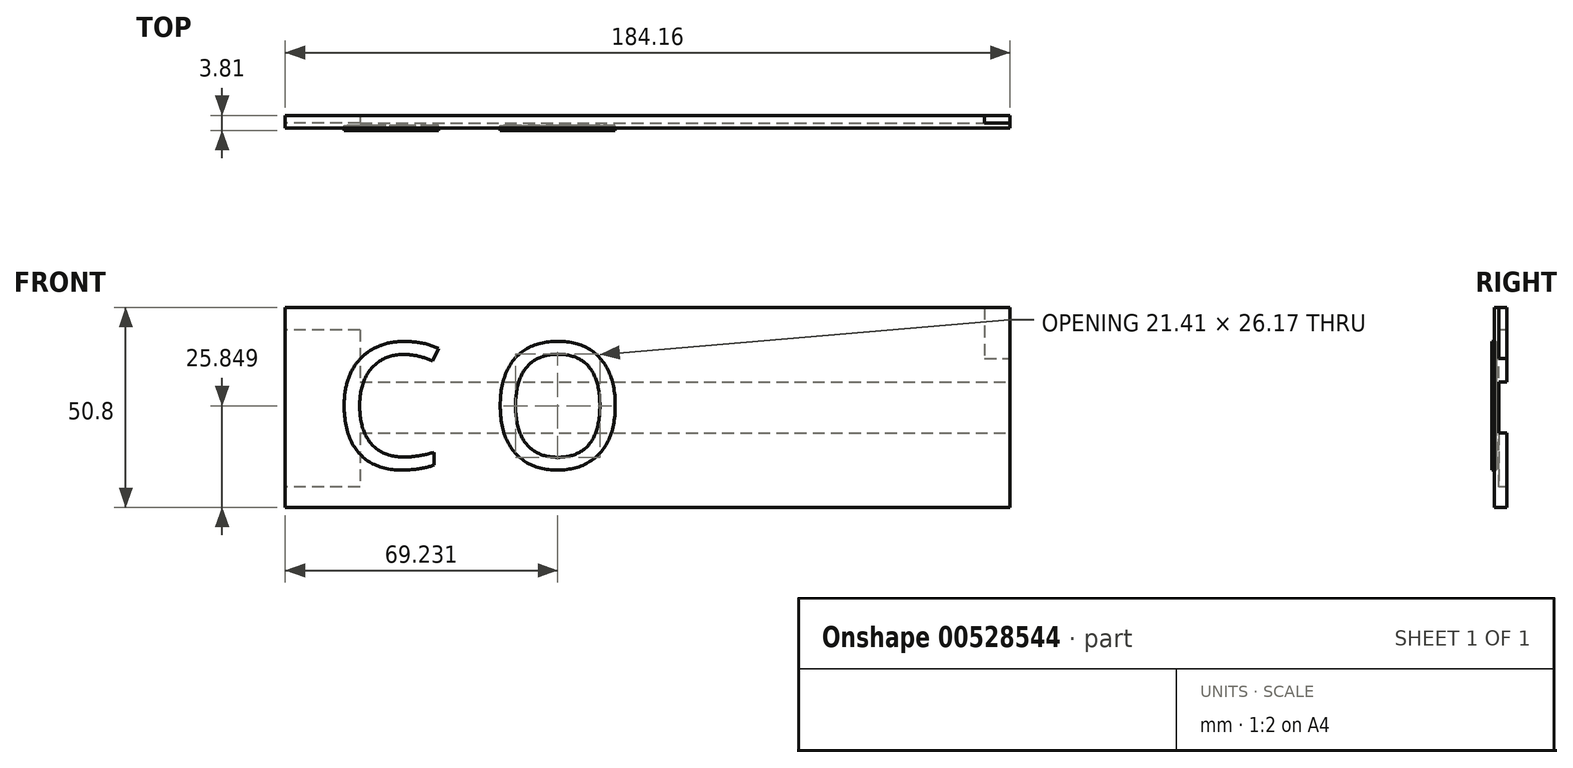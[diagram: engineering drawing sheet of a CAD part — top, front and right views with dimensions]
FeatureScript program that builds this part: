
annotation { "Feature Type Name" : "Feature", "Feature Type Description" : "" }
export const myFeature = defineFeature(function(context is Context, id is Id, definition is map)
    precondition{}
    {
        {
            var Q0;
            Q0=qCreatedBy(makeId("Front.planeOp"),FACE);
            var sketch = newSketch(context, id + "F0", { "sketchPlane" : qUnion([Q0])});
            skLineSegment(sketch, "E0.bottom", {"start": v(92.08, -25.4) * mm, "end": v(-92.08, -25.4) * mm});
            skLineSegment(sketch, "E0.top", {"start": v(92.08, 25.4) * mm, "end": v(-92.08, 25.4) * mm});
            skLineSegment(sketch, "E0.left", {"start": v(92.08, -25.4) * mm, "end": v(92.08, 25.4) * mm});
            skLineSegment(sketch, "E0.right", {"start": v(-92.08, -25.4) * mm, "end": v(-92.08, 25.4) * mm});
            skPoint(sketch, "E0.middle", {"position": v(0, 0) * mm});
            skSolve(sketch);
        }
        {
            var Q0;
            Q0=makeQuery(id+"F0.imprint","IMPRINT",FACE,{"disambiguationData":[TD([[makeQuery(id+"F0.imprint","IMPRINT",EDGE,{"derivedFrom":sQuery(id+"F0.wireOp",EDGE,"E0.bottom")}),-1.0]])]});
            var sketch = newSketch(context, id + "F1", { "sketchPlane" : qUnion([Q0])});
            skText(sketch, "E1", { "text": " C O ", "fontName": "OpenSans-Regular.ttf"});
            const initialGuessF1  = {"E1": [-0.0914, -0.01544, 1, 0, 0.03205]};
            skSetInitialGuess(sketch, initialGuessF1);
            skSolve(sketch);
        }
        {
            var Q0;
            Q0=qSketchRegion(id+"F1",true);
            extrude(context, id + "F2", {"entities" : qUnion([Q0]), "endBound" : BoundingType.SYMMETRIC, "depth" : 1.27 * mm, "offsetDistance" : 25.4 * mm});
        }
        {
            var Q0;
            Q0=makeQuery(id+"F0.imprint","IMPRINT",FACE,{"disambiguationData":[TD([[makeQuery(id+"F0.imprint","IMPRINT",EDGE,{"derivedFrom":sQuery(id+"F0.wireOp",EDGE,"E0.bottom")}),-1.0]])]});
            extrude(context, id + "F3", {"entities" : qUnion([Q0]), "oppositeDirection" : true, "depth" : 3.17 * mm, "offsetDistance" : 25.4 * mm});
        }
        {
            var Q0;
            Q0=makeQuery(id+"F3.opExtrude","CAP_FACE",FACE,{"disambiguationData":[OSD([sQuery(id+"F0.wireOp",EDGE,"E0.bottom"),sQuery(id+"F0.wireOp",EDGE,"E0.top"),sQuery(id+"F0.wireOp",EDGE,"E0.left"),sQuery(id+"F0.wireOp",EDGE,"E0.right")])],"isStart":false});
            var sketch = newSketch(context, id + "F4", { "sketchPlane" : qUnion([Q0])});
            skLineSegment(sketch, "E2.bottom", {"start": v(92.08, -6.5) * mm, "end": v(-92.08, -6.5) * mm});
            skLineSegment(sketch, "E2.top", {"start": v(92.08, 6.5) * mm, "end": v(-92.08, 6.5) * mm});
            skLineSegment(sketch, "E2.left", {"start": v(92.08, -6.5) * mm, "end": v(92.08, 6.5) * mm});
            skLineSegment(sketch, "E2.right", {"start": v(-92.08, -6.5) * mm, "end": v(-92.08, 6.5) * mm});
            skPoint(sketch, "E2.middle", {"position": v(0, 0) * mm});
            skSolve(sketch);
        }
        {
            var Q0;
            Q0=makeQuery(id+"F4.imprint","IMPRINT",FACE,{"disambiguationData":[TD([[makeQuery(id+"F4.imprint","IMPRINT",EDGE,{"derivedFrom":sQuery(id+"F4.wireOp",EDGE,"E2.bottom")}),-1.0]])]});
            extrude(context, id + "F5", {"entities" : qUnion([Q0]), "operationType" : NewBodyOperationType.REMOVE, "oppositeDirection" : true, "depth" : 1.9 * mm, "offsetDistance" : 25.4 * mm});
        }
        {
            var Q0;
            {var subQ0=sQuery(id+"F0.wireOp",EDGE,"E0.top");var subQ1=sQuery(id+"F0.wireOp",EDGE,"E0.left");var subQ2=sQuery(id+"F0.wireOp",EDGE,"E0.right");Q0=makeQuery(id+"FqrkbLo7UstCdvl_4.boolean.opBoolean","MERGE",FACE,{"derivedFrom":[makeQuery(id+"F5.boolean.opBoolean","SPLIT",FACE,{"disambiguationData":[TD([makeQuery(id+"F3.opExtrude","SWEPT_FACE",FACE,{"disambiguationData":[OSD([subQ0])]})])],"derivedFrom":makeQuery(id+"F3.opExtrude","CAP_FACE",FACE,{"disambiguationData":[OSD([sQuery(id+"F0.wireOp",EDGE,"E0.bottom"),subQ0,subQ1,subQ2])],"isStart":false})}),makeQuery(id+"FqrkbLo7UstCdvl_4.opExtrude","SWEPT_FACE",FACE,{"disambiguationData":[OSD([sQuery(id+"FWAWmwjFLXDaBw1_4.wireOp",EDGE,"giEz26mj-HDx3-KJuI-eFFI-Z6V8RftCm8Ms.top")])]})]});}
            var sketch = newSketch(context, id + "F6", { "sketchPlane" : qUnion([Q0])});
            skSolve(sketch);
        }
        {
            var Q0;
            Q0=makeQuery(id+"F5.boolean.opBoolean","COPY",FACE,{"derivedFrom":makeQuery(id+"F5.opExtrude","CAP_FACE",FACE,{"disambiguationData":[OSD([sQuery(id+"F4.wireOp",EDGE,"E2.bottom"),sQuery(id+"F4.wireOp",EDGE,"E2.top"),sQuery(id+"F4.wireOp",EDGE,"E2.left"),sQuery(id+"F4.wireOp",EDGE,"E2.right")])],"isStart":false})});
            var sketch = newSketch(context, id + "F7", { "sketchPlane" : qUnion([Q0])});
            skLineSegment(sketch, "E3.bottom", {"start": v(73.05, 19.74) * mm, "end": v(92.1, 19.74) * mm});
            skLineSegment(sketch, "E3.top", {"start": v(73.05, -20.15) * mm, "end": v(92.1, -20.15) * mm});
            skLineSegment(sketch, "E3.left", {"start": v(73.05, 19.74) * mm, "end": v(73.05, -20.15) * mm});
            skLineSegment(sketch, "E3.right", {"start": v(92.1, 19.74) * mm, "end": v(92.1, -20.15) * mm});
            skSolve(sketch);
        }
        {
            var Q0;
            Q0=qSketchRegion(id+"F7",true);
            extrude(context, id + "F8", {"entities" : qUnion([Q0]), "operationType" : NewBodyOperationType.REMOVE, "depth" : 13.2 * mm, "offsetDistance" : 25.4 * mm});
        }
        {
            var Q0;
            {var subQ0=sQuery(id+"F0.wireOp",EDGE,"E0.top");Q0=makeQuery(id+"F6.imprint","IMPRINT",FACE,{"disambiguationData":[TD([[makeQuery(id+"F6.imprint","IMPRINT",EDGE,{"derivedFrom":makeQuery(id+"F3.opExtrude","CAP_EDGE",EDGE,{"disambiguationData":[OSD([subQ0])],"isStart":false})}),-1.0]])]});}
            var sketch = newSketch(context, id + "F9", { "sketchPlane" : qUnion([Q0])});
            skLineSegment(sketch, "E4.bottom", {"start": v(-85.57, 25.45) * mm, "end": v(-92.17, 25.45) * mm});
            skLineSegment(sketch, "E4.top", {"start": v(-85.57, 12.5) * mm, "end": v(-92.17, 12.5) * mm});
            skLineSegment(sketch, "E4.left", {"start": v(-85.57, 25.45) * mm, "end": v(-85.57, 12.5) * mm});
            skLineSegment(sketch, "E4.right", {"start": v(-92.17, 25.45) * mm, "end": v(-92.17, 12.5) * mm});
            skSolve(sketch);
        }
        {
            var Q0;
            Q0=qSketchRegion(id+"F9",true);
            extrude(context, id + "F10", {"entities" : qUnion([Q0]), "operationType" : NewBodyOperationType.REMOVE, "oppositeDirection" : true, "depth" : 1.9 * mm, "offsetDistance" : 25.4 * mm});
        }
    });
